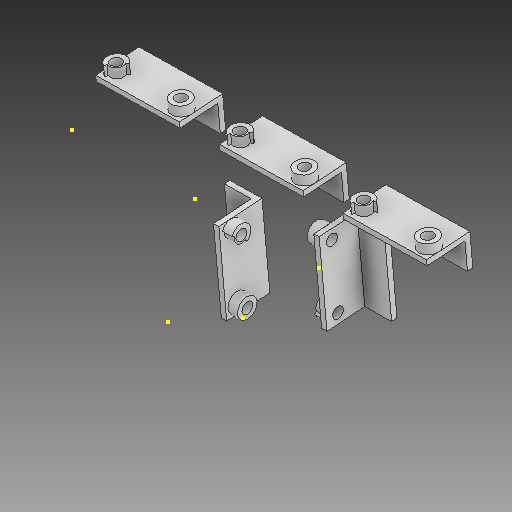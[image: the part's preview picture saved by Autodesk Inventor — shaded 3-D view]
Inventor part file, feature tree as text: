
AUTODESK INVENTOR PART (.ipt)
format: ipt  version: 2020 (Build 240168000, 168)  size: 222,208 bytes
history: native  units: mm
features: sketch x5, other x3
ambient origin geometry x8: Origin, YZ Plane, XZ Plane, XY Plane, X Axis, Y Axis, Z Axis, Center Point
bodies: Solid1 (feature_tree)
feature tree (8):
  other  "5DržačaLidara.ipt"
  other  "Solid1::5DržačaLidara.ipt"
  other  "TaggingFeature1"
  sketch  "Sketch8"
  sketch  "Sketch8_1"  dims[d0=10.0mm]
  sketch  "Sketch8_2"
  sketch  "Sketch8_3"
  sketch  "Sketch8_4"
